# Revit family: Haworth_K700_Stool
name_source: partatom
category: Furniture
revit_build: Autodesk Revit 2018 (Build: 20170223_1515(x64)
units: mm (PartAtom-declared; Revit-internal decimal feet)

## family parameters
Always vertical = Yes
Cut with Voids When Loaded = No
OmniClass Number = 23.40.70.14.64.21
OmniClass Title = Systems Furniture
Room Calculation Point = No
Shared = No
Work Plane-Based = No

## types (3) — shared parameters
Assembly Code = E2020200
Description = Haworth K700
Frame Finish = Haworth _ Metal _ Chrome
Manufacturer = Haworth
Model = K700
Revision Number = 5
Seat Finish = Haworth _ Fabric _ Tellure _ Steel 3A-39
Size = Verify Final Dim. w/ Haworth
URL = http://www.haworth.com
URL - Product = http://www.haworth.com
Warranty = http://www.haworth.com

## per-type parameters (varying)
| type | Actual Height | High | Low | Medium |
| K700 - 28h | 28" | Yes | No | No |
| K700 - 24h | 24" | No | No | Yes |
| K700 - 18h | 18" | No | Yes | No |

## geometry (parser evidence)
native form markers: Sweep x5
no freeform markers — native parametric forms only
